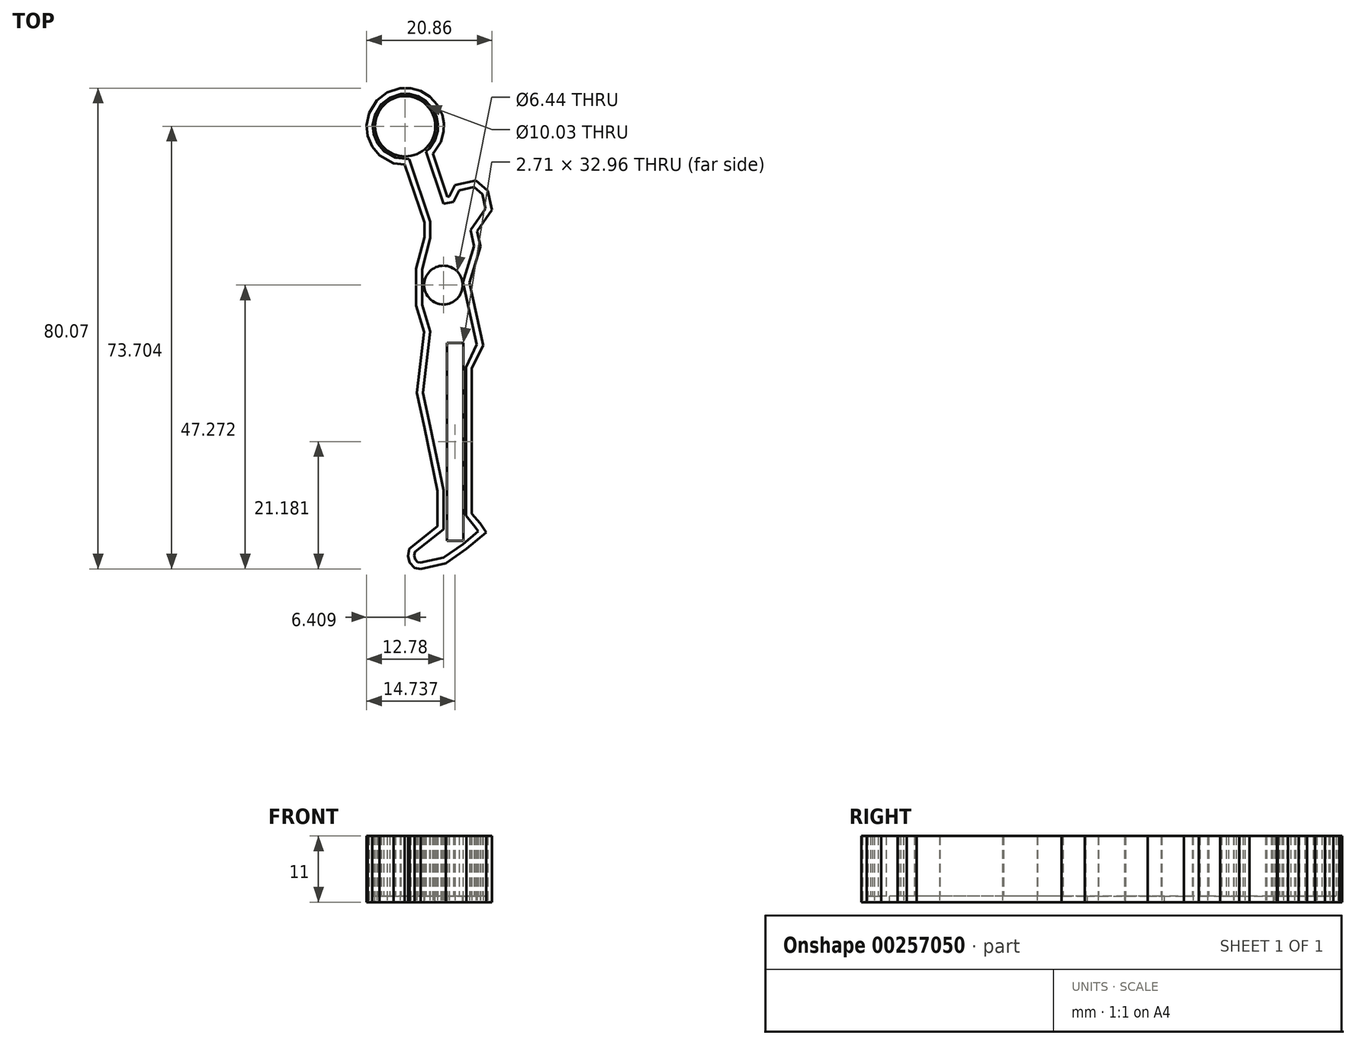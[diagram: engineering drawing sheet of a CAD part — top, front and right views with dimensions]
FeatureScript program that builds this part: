
annotation { "Feature Type Name" : "Feature", "Feature Type Description" : "" }
export const myFeature = defineFeature(function(context is Context, id is Id, definition is map)
    precondition{}
    {
        {
            var Q0;
            Q0=qCreatedBy(makeId("Top.planeOp"),FACE);
            var sketch = newSketch(context, id + "F0", { "sketchPlane" : qUnion([Q0])});
            skLineSegment(sketch, "E0", {"start": v(-5.71, 28.73) * mm, "end": v(-2.18, 18.31) * mm});
            skLineSegment(sketch, "E1", {"start": v(-2.18, 18.31) * mm, "end": v(-2.18, 15.57) * mm});
            skLineSegment(sketch, "E2", {"start": v(-2.18, 15.57) * mm, "end": v(-3.55, 10.37) * mm});
            skLineSegment(sketch, "E3", {"start": v(-3.55, 10.37) * mm, "end": v(-3.55, 4.47) * mm});
            skLineSegment(sketch, "E4", {"start": v(-3.55, 4.47) * mm, "end": v(-2.18, 0) * mm});
            skLineSegment(sketch, "E5", {"start": v(-2.18, 0) * mm, "end": v(-3.41, -10.19) * mm});
            skLineSegment(sketch, "E6", {"start": v(-3.41, -10.19) * mm, "end": v(-2.18, -15.8) * mm});
            skLineSegment(sketch, "E7", {"start": v(-2.18, -15.8) * mm, "end": v(0, -26.42) * mm});
            skLineSegment(sketch, "E8", {"start": v(0, -26.42) * mm, "end": v(0, -29.9) * mm});
            skLineSegment(sketch, "E9", {"start": v(0, -32.95) * mm, "end": v(-4.75, -36.73) * mm});
            skLineSegment(sketch, "E10", {"start": v(-3.41, -38.42) * mm, "end": v(0, -37.67) * mm});
            skLineSegment(sketch, "E11", {"start": v(0, -37.67) * mm, "end": v(3.23, -35.42) * mm});
            skLineSegment(sketch, "E12", {"start": v(3.74, -15.24) * mm, "end": v(3.74, -5.95) * mm});
            skLineSegment(sketch, "E13", {"start": v(3.74, -5.95) * mm, "end": v(5.56, -2.18) * mm});
            skLineSegment(sketch, "E14", {"start": v(5.56, -2.18) * mm, "end": v(5.08, 0) * mm});
            skLineSegment(sketch, "E15", {"start": v(5.08, 0) * mm, "end": v(4.31, 3.48) * mm});
            skLineSegment(sketch, "E16", {"start": v(4.31, 3.48) * mm, "end": v(3.28, 8.2) * mm});
            skLineSegment(sketch, "E17", {"start": v(3.28, 8.2) * mm, "end": v(5.12, 14.23) * mm});
            skLineSegment(sketch, "E18", {"start": v(5.12, 14.23) * mm, "end": v(4.53, 16.9) * mm});
            skLineSegment(sketch, "E19", {"start": v(4.53, 16.9) * mm, "end": v(7, 20.47) * mm});
            skLineSegment(sketch, "E20", {"start": v(7, 20.47) * mm, "end": v(6.48, 22.87) * mm});
            skLineSegment(sketch, "E21", {"start": v(6.48, 22.87) * mm, "end": v(5.12, 24.06) * mm});
            skLineSegment(sketch, "E22", {"start": v(5.12, 24.06) * mm, "end": v(2.63, 23.51) * mm});
            skLineSegment(sketch, "E23", {"start": v(2.63, 23.51) * mm, "end": v(1.64, 21.62) * mm});
            skLineSegment(sketch, "E24", {"start": v(1.64, 21.62) * mm, "end": v(0, 21.26) * mm});
            skLineSegment(sketch, "E25", {"start": v(0, 21.26) * mm, "end": v(-2.89, 29.96) * mm});
            skLineSegment(sketch, "E26", {"start": v(0, -29.9) * mm, "end": v(0, -32.95) * mm});
            skLineSegment(sketch, "E27", {"start": v(-5.71, 28.73) * mm, "end": v(-8, 28.98) * mm});
            skLineSegment(sketch, "E28", {"start": v(-8, 28.98) * mm, "end": v(-9.97, 30.11) * mm});
            skLineSegment(sketch, "E29", {"start": v(-9.97, 30.11) * mm, "end": v(-10.98, 31.33) * mm});
            skLineSegment(sketch, "E30", {"start": v(-10.98, 31.33) * mm, "end": v(-11.61, 32.84) * mm});
            skLineSegment(sketch, "E31", {"start": v(-11.61, 32.84) * mm, "end": v(-11.77, 34.33) * mm});
            skLineSegment(sketch, "E32", {"start": v(-11.77, 34.33) * mm, "end": v(-11.44, 36.02) * mm});
            skLineSegment(sketch, "E33", {"start": v(-11.44, 36.02) * mm, "end": v(-10.34, 37.84) * mm});
            skLineSegment(sketch, "E34", {"start": v(-10.34, 37.84) * mm, "end": v(-8.92, 38.94) * mm});
            skLineSegment(sketch, "E35", {"start": v(-8.92, 38.94) * mm, "end": v(-7.08, 39.54) * mm});
            skLineSegment(sketch, "E36", {"start": v(-7.08, 39.54) * mm, "end": v(-5.6, 39.54) * mm});
            skLineSegment(sketch, "E37", {"start": v(-5.6, 39.54) * mm, "end": v(-4.22, 39.15) * mm});
            skLineSegment(sketch, "E38", {"start": v(-4.22, 39.15) * mm, "end": v(-2.89, 38.35) * mm});
            skLineSegment(sketch, "E39", {"start": v(-2.89, 38.35) * mm, "end": v(-1.82, 37.16) * mm});
            skLineSegment(sketch, "E40", {"start": v(-1.82, 37.16) * mm, "end": v(-1.15, 35.75) * mm});
            skLineSegment(sketch, "E41", {"start": v(-1.15, 35.75) * mm, "end": v(-0.93, 34.61) * mm});
            skLineSegment(sketch, "E42", {"start": v(-0.93, 34.61) * mm, "end": v(-0.96, 33.44) * mm});
            skLineSegment(sketch, "E43", {"start": v(-0.96, 33.44) * mm, "end": v(-1.38, 31.95) * mm});
            skLineSegment(sketch, "E44", {"start": v(-1.38, 31.95) * mm, "end": v(-2.33, 30.5) * mm});
            skLineSegment(sketch, "E45", {"start": v(-2.33, 30.5) * mm, "end": v(-2.89, 29.96) * mm});
            skLineSegment(sketch, "E46", {"start": v(-3.41, -38.42) * mm, "end": v(-3.82, -38.5) * mm});
            skLineSegment(sketch, "E47", {"start": v(-3.82, -38.5) * mm, "end": v(-4.3, -38.42) * mm});
            skLineSegment(sketch, "E48", {"start": v(-4.3, -38.42) * mm, "end": v(-4.7, -38) * mm});
            skLineSegment(sketch, "E49", {"start": v(-4.7, -38) * mm, "end": v(-4.85, -37.34) * mm});
            skLineSegment(sketch, "E50", {"start": v(-4.85, -37.34) * mm, "end": v(-4.75, -36.73) * mm});
            skLineSegment(sketch, "E51", {"start": v(4.79, -33.22) * mm, "end": v(4.82, -33.27) * mm});
            skLineSegment(sketch, "E52", {"start": v(3.74, -15.24) * mm, "end": v(3.74, -22.77) * mm});
            skLineSegment(sketch, "E53", {"start": v(3.74, -22.77) * mm, "end": v(3.74, -28.84) * mm});
            skLineSegment(sketch, "E54", {"start": v(3.74, -28.84) * mm, "end": v(3.74, -30.1) * mm});
            skLineSegment(sketch, "E55", {"start": v(3.74, -30.1) * mm, "end": v(3.74, -30.7) * mm});
            skLineSegment(sketch, "E56", {"start": v(3.74, -30.7) * mm, "end": v(5.3, -32.55) * mm});
            skLineSegment(sketch, "E57", {"start": v(5.3, -32.55) * mm, "end": v(5.8, -33.27) * mm});
            skLineSegment(sketch, "E58", {"start": v(5.8, -33.27) * mm, "end": v(3.23, -35.42) * mm});
            skSolve(sketch);
        }
        {
            var Q0;
            Q0=makeQuery(id+"F0.imprint","IMPRINT",FACE,{"disambiguationData":[TD([[makeQuery(id+"F0.imprint","IMPRINT",EDGE,{"derivedFrom":sQuery(id+"F0.wireOp",EDGE,"E0")}),1.0]])]});
            extrude(context, id + "F1", {"entities" : qUnion([Q0]), "depth" : 10 * mm});
        }
        {
            var Q0;
            Q0=makeQuery(id+"F1.opExtrude","CAP_FACE",FACE,{"disambiguationData":[OSD([sQuery(id+"F0.wireOp",EDGE,"E0"),sQuery(id+"F0.wireOp",EDGE,"E1"),sQuery(id+"F0.wireOp",EDGE,"E2"),sQuery(id+"F0.wireOp",EDGE,"E3"),sQuery(id+"F0.wireOp",EDGE,"E4"),sQuery(id+"F0.wireOp",EDGE,"E5"),sQuery(id+"F0.wireOp",EDGE,"E6"),sQuery(id+"F0.wireOp",EDGE,"E7"),sQuery(id+"F0.wireOp",EDGE,"E8"),sQuery(id+"F0.wireOp",EDGE,"E9"),sQuery(id+"F0.wireOp",EDGE,"w97T0TOw-6l8Q-ZajR-afi6-BgXT67dO3md0"),sQuery(id+"F0.wireOp",EDGE,"E10"),sQuery(id+"F0.wireOp",EDGE,"E11"),sQuery(id+"F0.wireOp",EDGE,"h0z5I9EL-Su9J-pTn8-ROkF-syBcGJboysGt"),sQuery(id+"F0.wireOp",EDGE,"LWH5GDxL-C8TP-FxOE-ypZX-RzmWzZoZxmDi"),sQuery(id+"F0.wireOp",EDGE,"lYiemvI0-lylr-mDEu-hW78-VmD73YXohHGD"),sQuery(id+"F0.wireOp",EDGE,"JAOvIleB-zqoO-Pfpo-gvQq-f6Djw42w0i0H"),sQuery(id+"F0.wireOp",EDGE,"UkqNxwF7-2j3a-sAi4-Exze-yqudwmwT2JkB"),sQuery(id+"F0.wireOp",EDGE,"tRyYEXEU-gWm4-jD3q-fhcb-tbuY6M4T3QK7"),sQuery(id+"F0.wireOp",EDGE,"E12"),sQuery(id+"F0.wireOp",EDGE,"E13"),sQuery(id+"F0.wireOp",EDGE,"E14"),sQuery(id+"F0.wireOp",EDGE,"E15"),sQuery(id+"F0.wireOp",EDGE,"E16"),sQuery(id+"F0.wireOp",EDGE,"E17"),sQuery(id+"F0.wireOp",EDGE,"E18"),sQuery(id+"F0.wireOp",EDGE,"E19"),sQuery(id+"F0.wireOp",EDGE,"E20"),sQuery(id+"F0.wireOp",EDGE,"E21"),sQuery(id+"F0.wireOp",EDGE,"E22"),sQuery(id+"F0.wireOp",EDGE,"E23"),sQuery(id+"F0.wireOp",EDGE,"E24"),sQuery(id+"F0.wireOp",EDGE,"E25"),sQuery(id+"F0.wireOp",EDGE,"Jdc0OOBK-FAKV-ChgV-8UNj-7x0W1v9qKJCb"),sQuery(id+"F0.wireOp",EDGE,"uoE8jYEa-AGLA-ydIz-OY5x-GXcaaGzfI5Ja"),sQuery(id+"F0.wireOp",EDGE,"Ysal1UBa-ZwI8-fCr1-QwCk-aFjarvst0lzS"),sQuery(id+"F0.wireOp",EDGE,"vEsi4ZJv-jchG-zCw9-9ax6-6BhpsLBMRD7a"),sQuery(id+"F0.wireOp",EDGE,"dg4c5DIF-8UJf-KI3t-LVmu-de8wnh5wNTnI"),sQuery(id+"F0.wireOp",EDGE,"gQHcPAq1-NLca-cBd8-fJh8-wXJe7HIOwOpI"),sQuery(id+"F0.wireOp",EDGE,"bTd1aKqq-RjER-ucQp-1d5S-sXHndstxXtQr"),sQuery(id+"F0.wireOp",EDGE,"tEW69jBY-VK40-UxgB-4ueq-VAM0TVuKm5iq"),sQuery(id+"F0.wireOp",EDGE,"cnlFeOBb-XNxQ-isqV-e5rp-SadNojo8kUE7"),sQuery(id+"F0.wireOp",EDGE,"PAXINxjD-mH3p-Xw8v-Qy2n-7pSnkqZV94r9"),sQuery(id+"F0.wireOp",EDGE,"E26")])],"isStart":false});
            shell(context, id + "F2", {"entities" : qUnion([Q0]), "thickness" : 1 * mm, "oppositeDirection" : true});
        }
        {
            var Q0;
            Q0=qCreatedBy(makeId("Top.planeOp"),FACE);
            var sketch = newSketch(context, id + "F3", { "sketchPlane" : qUnion([Q0])});
            skCircle(sketch, "E59", {"center": v(0, 7.74) * mm, "radius": 3.22 * mm});
            skSolve(sketch);
        }
        {
            var Q0;
            Q0 = qSketchRegion(id + "F3", true);
            extrude(context, id + "F4", {"entities" : qUnion([Q0]), "operationType" : NewBodyOperationType.REMOVE, "oppositeDirection" : true, "depth" : 25.4 * mm});
        }
        {
            var Q0;
            Q0=qCreatedBy(makeId("Top.planeOp"),FACE);
            var sketch = newSketch(context, id + "F5", { "sketchPlane" : qUnion([Q0])});
            skCircle(sketch, "E60", {"center": v(-6.37, 34.17) * mm, "radius": 5.01 * mm});
            skSolve(sketch);
        }
        {
            var Q0;
            Q0 = qSketchRegion(id + "F5", true);
            extrude(context, id + "F6", {"entities" : qUnion([Q0]), "operationType" : NewBodyOperationType.REMOVE, "oppositeDirection" : true, "depth" : 25.4 * mm});
        }
        {
            var Q0;
            Q0=qCreatedBy(makeId("Top.planeOp"),FACE);
            var sketch = newSketch(context, id + "F7", { "sketchPlane" : qUnion([Q0])});
            skLineSegment(sketch, "E61.bottom", {"start": v(0.6, -1.87) * mm, "end": v(3.31, -1.87) * mm});
            skLineSegment(sketch, "E61.top", {"start": v(0.6, -34.83) * mm, "end": v(3.31, -34.83) * mm});
            skLineSegment(sketch, "E61.left", {"start": v(0.6, -1.87) * mm, "end": v(0.6, -34.83) * mm});
            skLineSegment(sketch, "E61.right", {"start": v(3.31, -1.87) * mm, "end": v(3.31, -34.83) * mm});
            skSolve(sketch);
        }
        {
            var Q0;
            Q0 = qSketchRegion(id + "F7", true);
            extrude(context, id + "F8", {"entities" : qUnion([Q0]), "operationType" : NewBodyOperationType.REMOVE, "oppositeDirection" : true, "depth" : 25 * mm});
        }
    });
